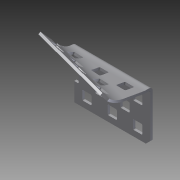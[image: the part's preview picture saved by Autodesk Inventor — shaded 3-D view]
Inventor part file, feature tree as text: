
AUTODESK INVENTOR PART (.ipt)
format: ipt  version: 2014 SP1 (Build 180222100, 222)  size: 1,169,408 bytes
history: native  units: in
note: dims shown in document units (in); Inventor stores cm internally (conversion verified against a paired STEP export)
features: other x3, sketch x3, imported_body x1, extrude x1
ambient origin geometry x8: Origin, YZ Plane, XZ Plane, XY Plane, X Axis, Y Axis, Z Axis, Center Point
bodies: Body1 (feature_tree)
feature tree (8):
  parser-record x1  (decoder bookkeeping rows leaked as tree rows — omitted from the tree; the rows remain in map.json)
  imported_body  "Base1"
  extrude  "Extrusion1"  Depth=6.0in
  other  "Bend Part1"
  other  "Bend Part2"
  sketch  "Sketch1"  dims[d0=1.0in d1=0.0in d2=6.0in]
  sketch  "Sketch3"  dims[d3=0.5in d4=0.2749in]
  sketch  "Sketch4"  dims[d5=0.5in d6=0.0687in]
